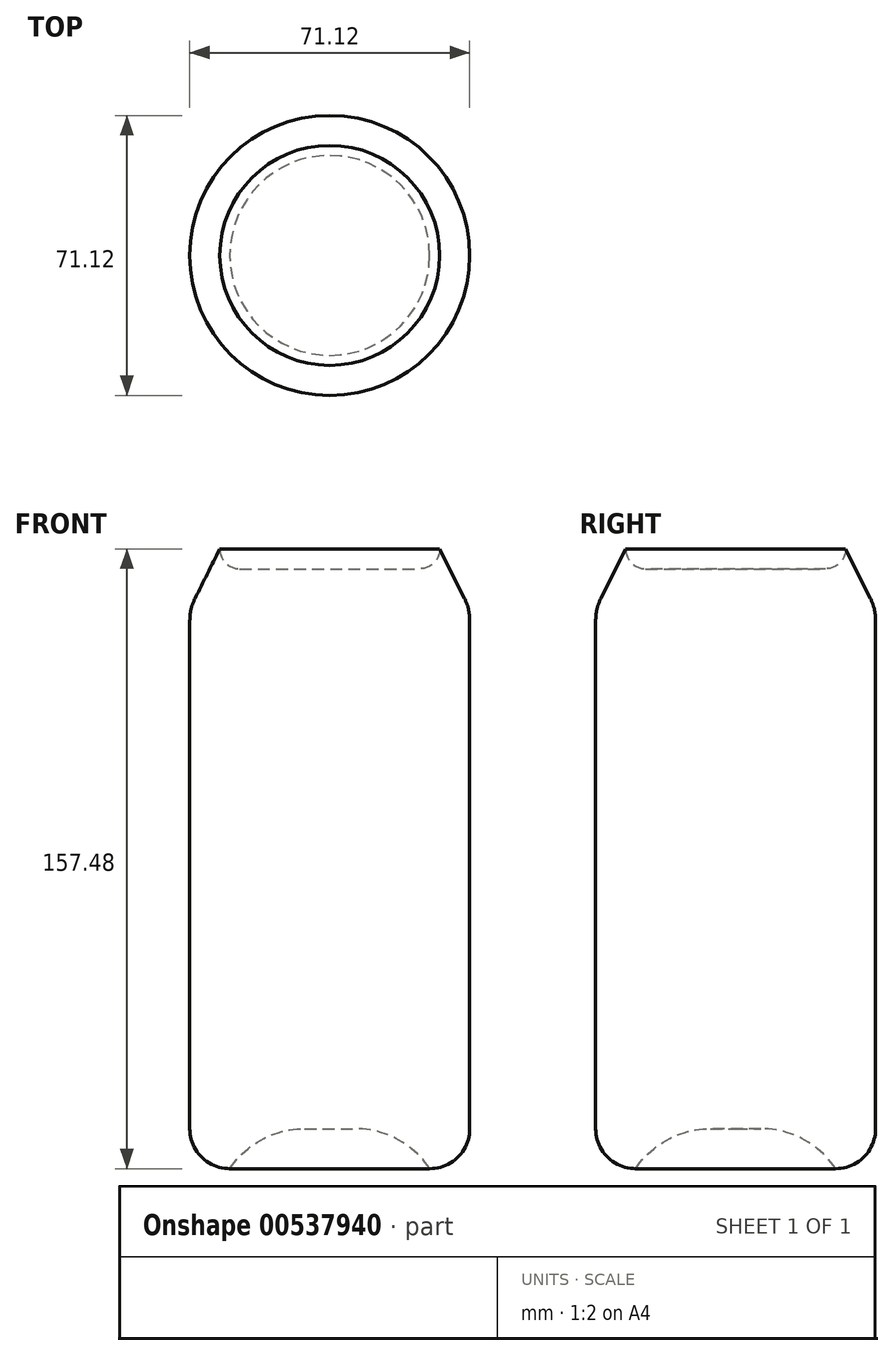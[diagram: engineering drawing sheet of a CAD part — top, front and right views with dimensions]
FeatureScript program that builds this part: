
annotation { "Feature Type Name" : "Feature", "Feature Type Description" : "" }
export const myFeature = defineFeature(function(context is Context, id is Id, definition is map)
    precondition{}
    {
        {
            var Q0;
            Q0=qCreatedBy(makeId("Front.planeOp"),FACE);
            var sketch = newSketch(context, id + "F0", { "sketchPlane" : qUnion([Q0])});
            skLineSegment(sketch, "E0.bottom", {"start": v(0, 0) * mm, "end": v(35.56, 0) * mm});
            skLineSegment(sketch, "E0.top", {"start": v(0, 63.5) * mm, "end": v(35.56, 63.5) * mm});
            skLineSegment(sketch, "E0.left", {"start": v(0, 0) * mm, "end": v(0, 63.5) * mm});
            skLineSegment(sketch, "E0.right", {"start": v(35.56, 0) * mm, "end": v(35.56, 63.5) * mm});
            skLineSegment(sketch, "E1.MirrorCS", {"start": v(35.56, 0) * mm, "end": v(35.56, -63.5) * mm});
            skLineSegment(sketch, "E2.MirrorCS", {"start": v(0, -63.5) * mm, "end": v(35.56, -63.5) * mm});
            skLineSegment(sketch, "E3.MirrorCS", {"start": v(0, 0) * mm, "end": v(0, -63.5) * mm});
            skLineSegment(sketch, "E4.top", {"start": v(0, 83.82) * mm, "end": v(35.56, 83.82) * mm});
            skLineSegment(sketch, "E4.left", {"start": v(0, 63.5) * mm, "end": v(0, 83.82) * mm});
            skLineSegment(sketch, "E4.right", {"start": v(35.56, 63.5) * mm, "end": v(35.56, 83.82) * mm});
            skLineSegment(sketch, "E5.top", {"start": v(0, -73.66) * mm, "end": v(35.56, -73.66) * mm});
            skLineSegment(sketch, "E5.left", {"start": v(0, -63.5) * mm, "end": v(0, -73.66) * mm});
            skLineSegment(sketch, "E5.right", {"start": v(35.56, -63.5) * mm, "end": v(35.56, -73.66) * mm});
            skSolve(sketch);
        }
        {
            var Q0;
            Q0 = qSketchRegion(id + "F0", true);
            var Q1;
            Q1=sQuery(id+"F0.wireOp",EDGE,"E0.left");
            revolve(context, id + "F1", {"entities" : qUnion([Q0]), "axis" : qUnion([Q1]), "revolveType" : RevolveType.FULL});
        }
        {
            var Q0;
            Q0=makeQuery(id+"F1.opRevolve","SWEPT_EDGE",EDGE,{"disambiguationData":[OSD([sQuery(id+"F0.wireOp",EDGE,"E4.top"),sQuery(id+"F0.wireOp",EDGE,"E4.right")])]});
            chamfer(context, id + "F2", {"entities" : qUnion([Q0]), "chamferType" : ChamferType.TWO_OFFSETS, "width1" : 15.24 * mm, "oppositeDirection" : false, "width2" : 7.62 * mm, "tangentPropagation" : true});
        }
        {
            var Q0;
            {var subQ0=sQuery(id+"F0.wireOp",EDGE,"E4.right");Q0=makeQuery(id+"F2.opChamfer","BLEND_EDGE",EDGE,{"blendedFrom":[makeQuery(id+"F1.opRevolve","SWEPT_EDGE",EDGE,{"disambiguationData":[OSD([sQuery(id+"F0.wireOp",EDGE,"E4.top"),subQ0])]}),makeQuery(id+"F1.opRevolve","SWEPT_FACE",FACE,{"disambiguationData":[OSD([sQuery(id+"F0.wireOp",EDGE,"E0.right"),sQuery(id+"F0.wireOp",EDGE,"E1.MirrorCS"),subQ0,sQuery(id+"F0.wireOp",EDGE,"E5.right")])]})],"blendedInto":[makeQuery(id+"F1.opRevolve","SWEPT_FACE",FACE,{"disambiguationData":[OSD([sQuery(id+"F0.wireOp",EDGE,"E0.right"),sQuery(id+"F0.wireOp",EDGE,"E1.MirrorCS"),subQ0,sQuery(id+"F0.wireOp",EDGE,"E5.right")])]})]});}
            fillet(context, id + "F3", {"entities" : qUnion([Q0]), "radius" : 12.7 * mm, "tangentPropagation" : true, "allowEdgeOverflow" : false});
        }
        {
            var Q0;
            Q0=makeQuery(id+"F1.opRevolve","SWEPT_FACE",FACE,{"disambiguationData":[OSD([sQuery(id+"F0.wireOp",EDGE,"E4.top")])]});
            extrude(context, id + "F4", {"entities" : qUnion([Q0]), "operationType" : NewBodyOperationType.REMOVE, "oppositeDirection" : true, "depth" : 5.08 * mm, "offsetDistance" : 25.4 * mm});
        }
        {
            var Q0;
            Q0=makeQuery(id+"F4.boolean.opBoolean","COPY",EDGE,{"derivedFrom":makeQuery(id+"F4.opExtrude","CAP_EDGE",EDGE,{"disambiguationData":[OSD([sQuery(id+"F0.wireOp",EDGE,"E4.top"),sQuery(id+"F0.wireOp",EDGE,"E4.right")])],"isStart":false})});
            fillet(context, id + "F5", {"entities" : qUnion([Q0]), "radius" : 5.08 * mm, "tangentPropagation" : true, "allowEdgeOverflow" : false});
        }
        {
            var Q0;
            Q0=makeQuery(id+"F1.opRevolve","SWEPT_EDGE",EDGE,{"disambiguationData":[OSD([sQuery(id+"F0.wireOp",EDGE,"E5.top"),sQuery(id+"F0.wireOp",EDGE,"E5.right")])]});
            fillet(context, id + "F6", {"entities" : qUnion([Q0]), "radius" : 10.16 * mm, "tangentPropagation" : true, "allowEdgeOverflow" : false});
        }
        {
            var Q0;
            Q0=makeQuery(id+"F1.opRevolve","SWEPT_FACE",FACE,{"disambiguationData":[OSD([sQuery(id+"F0.wireOp",EDGE,"E5.top")])]});
            extrude(context, id + "F7", {"entities" : qUnion([Q0]), "operationType" : NewBodyOperationType.REMOVE, "oppositeDirection" : true, "depth" : 10.16 * mm, "offsetDistance" : 25.4 * mm});
        }
        {
            var Q0;
            Q0=makeQuery(id+"F7.boolean.opBoolean","COPY",EDGE,{"derivedFrom":makeQuery(id+"F7.opExtrude","CAP_EDGE",EDGE,{"disambiguationData":[OSD([sQuery(id+"F0.wireOp",EDGE,"E5.top"),sQuery(id+"F0.wireOp",EDGE,"E5.right")])],"isStart":false})});
            fillet(context, id + "F8", {"entities" : qUnion([Q0]), "radius" : 22.86 * mm, "tangentPropagation" : true, "allowEdgeOverflow" : false});
        }
    });
